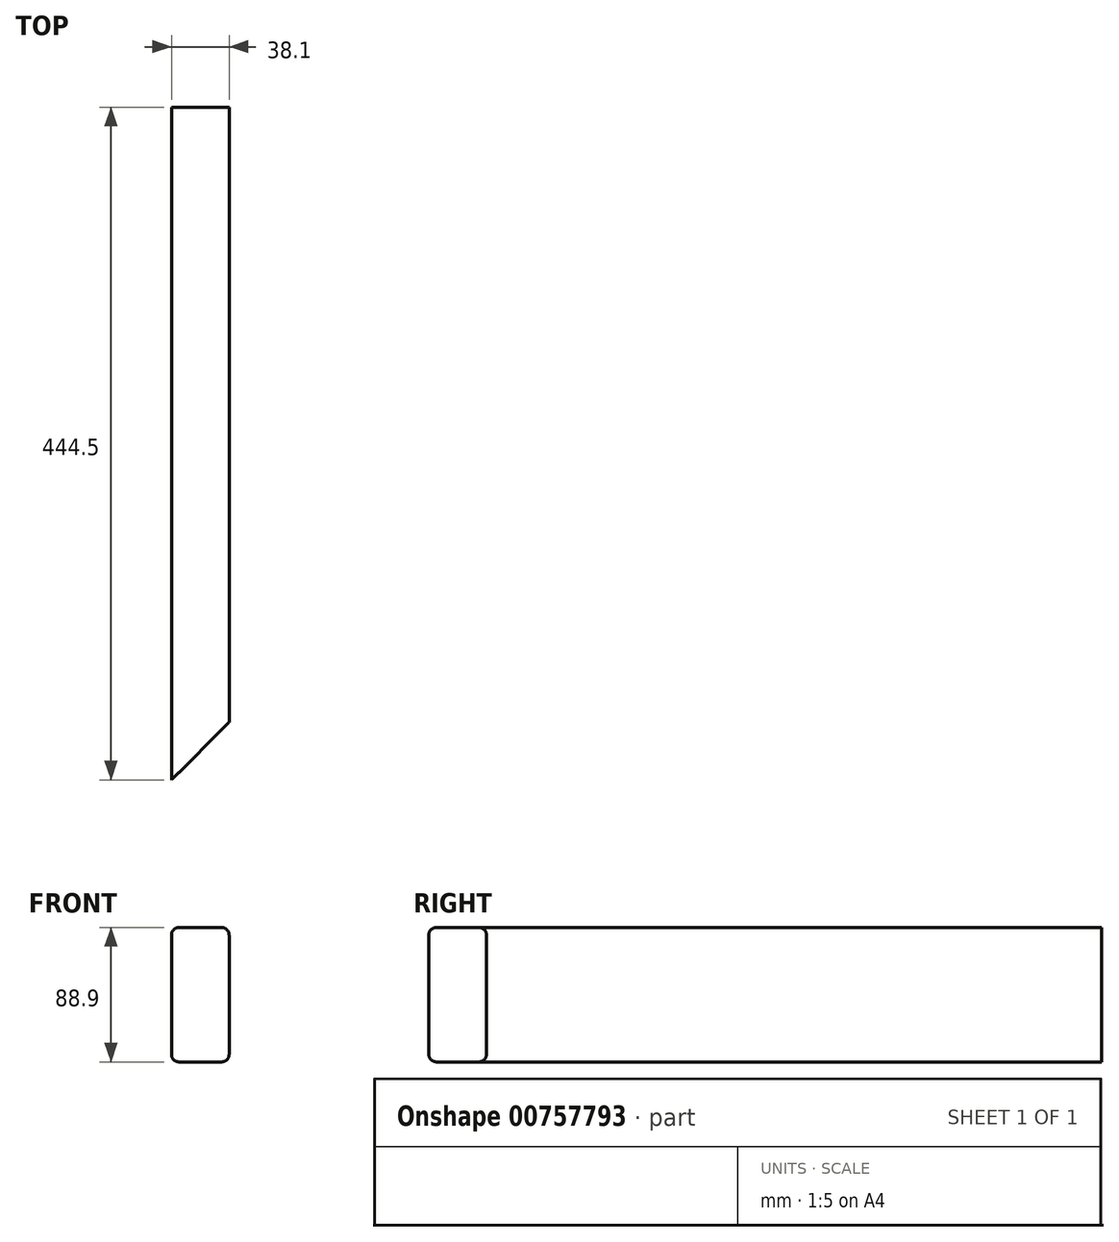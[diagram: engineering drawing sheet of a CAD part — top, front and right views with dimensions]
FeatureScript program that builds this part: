
annotation { "Feature Type Name" : "Feature", "Feature Type Description" : "" }
export const myFeature = defineFeature(function(context is Context, id is Id, definition is map)
    precondition{}
    {
        {
            var Q0;
            Q0=qCreatedBy(makeId("Front.planeOp"),FACE);
            var sketch = newSketch(context, id + "F0", { "sketchPlane" : qUnion([Q0])});
            skLineSegment(sketch, "E0.bottom", {"start": v(-16.21, 42.82) * mm, "end": v(21.89, 42.82) * mm});
            skLineSegment(sketch, "E0.top", {"start": v(-16.21, -46.08) * mm, "end": v(21.89, -46.08) * mm});
            skLineSegment(sketch, "E0.left", {"start": v(-16.21, 42.82) * mm, "end": v(-16.21, -46.08) * mm});
            skLineSegment(sketch, "E0.right", {"start": v(21.89, 42.82) * mm, "end": v(21.89, -46.08) * mm});
            skSolve(sketch);
        }
        {
            var Q0;
            Q0=makeQuery(id+"F0.imprint","IMPRINT",FACE,{"disambiguationData":[TD([[makeQuery(id+"F0.imprint","IMPRINT",EDGE,{"derivedFrom":sQuery(id+"F0.wireOp",EDGE,"E0.bottom")}),-1.0]])]});
            extrude(context, id + "F1", {"entities" : qUnion([Q0]), "depth" : 444.5 * mm, "offsetDistance" : 25.4 * mm});
        }
        {
            var Q0;
            Q0=makeQuery(id+"F1.opExtrude","SWEPT_FACE",FACE,{"disambiguationData":[OSD([sQuery(id+"F0.wireOp",EDGE,"E0.bottom")])]});
            var sketch = newSketch(context, id + "F2", { "sketchPlane" : qUnion([Q0])});
            skLineSegment(sketch, "E1", {"start": v(-16.21, -444.5) * mm, "end": v(21.89, -406.4) * mm});
            skLineSegment(sketch, "E2", {"start": v(21.89, -406.4) * mm, "end": v(21.89, -444.5) * mm});
            skLineSegment(sketch, "E3", {"start": v(21.89, -444.5) * mm, "end": v(-16.21, -444.5) * mm});
            skSolve(sketch);
        }
        {
            var Q0;
            Q0=makeQuery(id+"F2.imprint","IMPRINT",FACE,{"disambiguationData":[TD([[makeQuery(id+"F2.imprint","IMPRINT",EDGE,{"derivedFrom":sQuery(id+"F2.wireOp",EDGE,"E1")}),-1.0]])]});
            extrude(context, id + "F3", {"entities" : qUnion([Q0]), "operationType" : NewBodyOperationType.REMOVE, "oppositeDirection" : true, "depth" : 88.9 * mm, "offsetDistance" : 25.4 * mm});
        }
        {
            var Q0;
            Q0=makeQuery(id+"F1.opExtrude","SWEPT_EDGE",EDGE,{"disambiguationData":[OSD([sQuery(id+"F0.wireOp",EDGE,"E0.bottom"),sQuery(id+"F0.wireOp",EDGE,"E0.right")])]});
            var Q1;
            Q1=makeQuery(id+"F1.opExtrude","SWEPT_EDGE",EDGE,{"disambiguationData":[OSD([sQuery(id+"F0.wireOp",EDGE,"E0.top"),sQuery(id+"F0.wireOp",EDGE,"E0.right")])]});
            var Q2;
            Q2=makeQuery(id+"F1.opExtrude","SWEPT_EDGE",EDGE,{"disambiguationData":[OSD([sQuery(id+"F0.wireOp",EDGE,"E0.bottom"),sQuery(id+"F0.wireOp",EDGE,"E0.left")])]});
            var Q3;
            Q3=makeQuery(id+"F1.opExtrude","SWEPT_EDGE",EDGE,{"disambiguationData":[OSD([sQuery(id+"F0.wireOp",EDGE,"E0.top"),sQuery(id+"F0.wireOp",EDGE,"E0.left")])]});
            fillet(context, id + "F4", {"entities" : qUnion([Q0, Q1, Q2, Q3]), "radius" : 5.08 * mm, "tangentPropagation" : true, "allowEdgeOverflow" : false});
        }
    });
